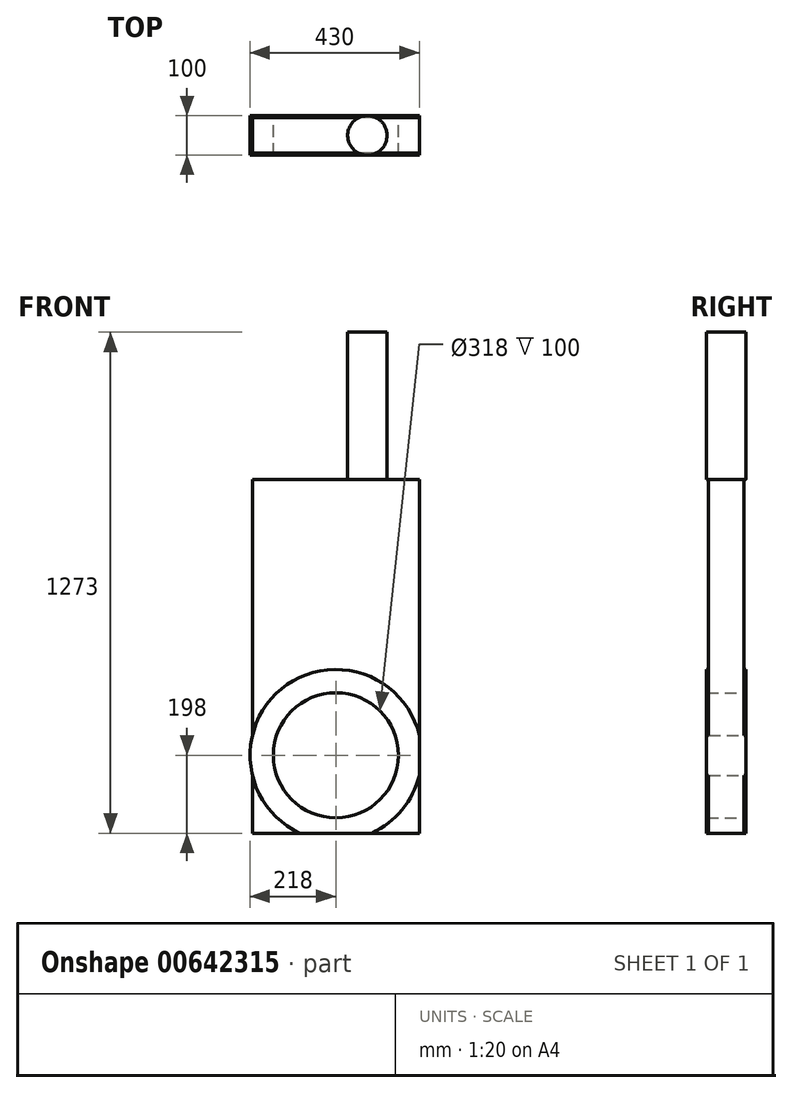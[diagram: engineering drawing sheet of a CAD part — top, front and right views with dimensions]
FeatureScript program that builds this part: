
annotation { "Feature Type Name" : "Feature", "Feature Type Description" : "" }
export const myFeature = defineFeature(function(context is Context, id is Id, definition is map)
    precondition{}
    {
        {
            var Q0;
            Q0=qCreatedBy(makeId("Front.planeOp"),FACE);
            var sketch = newSketch(context, id + "F0", { "sketchPlane" : qUnion([Q0])});
            skLineSegment(sketch, "E0.bottom", {"start": v(212, -449.5) * mm, "end": v(-212, -449.5) * mm});
            skLineSegment(sketch, "E0.top", {"start": v(212, 449.5) * mm, "end": v(-212, 449.5) * mm});
            skLineSegment(sketch, "E0.left", {"start": v(212, -449.5) * mm, "end": v(212, 449.5) * mm});
            skLineSegment(sketch, "E0.right", {"start": v(-212, -449.5) * mm, "end": v(-212, 449.5) * mm});
            skPoint(sketch, "E0.middle", {"position": v(0, 0) * mm});
            skSolve(sketch);
        }
        {
            var Q0;
            Q0=makeQuery(id+"F0.imprint","IMPRINT",FACE,{"disambiguationData":[TD([[makeQuery(id+"F0.imprint","IMPRINT",EDGE,{"derivedFrom":sQuery(id+"F0.wireOp",EDGE,"E0.bottom")}),-1.0]])]});
            extrude(context, id + "F1", {"entities" : qUnion([Q0]), "depth" : 90 * mm, "offsetDistance" : 25 * mm});
        }
        {
            var Q0;
            Q0=makeQuery(id+"F1.opExtrude","CAP_FACE",FACE,{"disambiguationData":[OSD([sQuery(id+"F0.wireOp",EDGE,"E0.bottom"),sQuery(id+"F0.wireOp",EDGE,"E0.top"),sQuery(id+"F0.wireOp",EDGE,"E0.left"),sQuery(id+"F0.wireOp",EDGE,"E0.right")])],"isStart":false});
            var sketch = newSketch(context, id + "F2", { "sketchPlane" : qUnion([Q0])});
            skCircle(sketch, "E1", {"center": v(0, -251.5) * mm, "radius": 218 * mm});
            skCircle(sketch, "E2", {"center": v(0, -251.5) * mm, "radius": 159 * mm});
            skSolve(sketch);
        }
        {
            var Q0;
            {var subQ0=sQuery(id+"F2.wireOp",EDGE,"E1");var subQ1=makeQuery(id+"F1.opExtrude","CAP_EDGE",EDGE,{"disambiguationData":[OSD([sQuery(id+"F0.wireOp",EDGE,"E0.right")])],"isStart":false});var subQ2=makeQuery(id+"F2.imprint","INTERSECT",VERTEX,{"disambiguationData":[OD(0.0)],"derivedFrom":[subQ1,subQ0]});Q0=makeQuery(id+"F2.imprint","IMPRINT",FACE,{"disambiguationData":[TD([[makeQuery(id+"F2.imprint","IMPRINT",EDGE,{"disambiguationData":[TD([[subQ2,-1.0]])],"derivedFrom":subQ0}),1.0]])]});}
            var Q1;
            Q1=makeQuery(id+"F2.imprint","IMPRINT",FACE,{"disambiguationData":[TD([[makeQuery(id+"F2.imprint","IMPRINT",EDGE,{"derivedFrom":sQuery(id+"F2.wireOp",EDGE,"E2")}),-1.0]])]});
            var Q2;
            {var subQ0=sQuery(id+"F2.wireOp",EDGE,"E1");var subQ1=makeQuery(id+"F1.opExtrude","CAP_EDGE",EDGE,{"disambiguationData":[OSD([sQuery(id+"F0.wireOp",EDGE,"E0.left")])],"isStart":false});var subQ2=makeQuery(id+"F2.imprint","INTERSECT",VERTEX,{"disambiguationData":[OD(0.0)],"derivedFrom":[subQ1,subQ0]});Q2=makeQuery(id+"F2.imprint","IMPRINT",FACE,{"disambiguationData":[TD([[makeQuery(id+"F2.imprint","IMPRINT",EDGE,{"disambiguationData":[TD([[subQ2,1.0]])],"derivedFrom":subQ0}),1.0]])]});}
            var Q3;
            {var subQ0=sQuery(id+"F2.wireOp",EDGE,"E1");var subQ1=makeQuery(id+"F1.opExtrude","CAP_EDGE",EDGE,{"disambiguationData":[OSD([sQuery(id+"F0.wireOp",EDGE,"E0.bottom")])],"isStart":false});var subQ2=makeQuery(id+"F2.imprint","INTERSECT",VERTEX,{"disambiguationData":[OD(0.0)],"derivedFrom":[subQ1,subQ0]});Q3=makeQuery(id+"F2.imprint","IMPRINT",FACE,{"disambiguationData":[TD([[makeQuery(id+"F2.imprint","IMPRINT",EDGE,{"disambiguationData":[TD([[subQ2,-1.0]])],"derivedFrom":subQ0}),1.0]])]});}
            extrude(context, id + "F3", {"entities" : qUnion([Q0, Q1, Q2, Q3]), "operationType" : NewBodyOperationType.ADD, "depth" : 5 * mm, "offsetDistance" : 25 * mm, "hasSecondDirection" : true, "secondDirectionOppositeDirection" : true, "secondDirectionDepth" : 95 * mm});
        }
        {
            var Q0;
            Q0=makeQuery(id+"F3.boolean.opBoolean","SPLIT",FACE,{"disambiguationData":[TD([makeQuery(id+"F3.opExtrude","SWEPT_FACE",FACE,{"disambiguationData":[OSD([sQuery(id+"F2.wireOp",EDGE,"E2")])]})])],"derivedFrom":makeQuery(id+"F1.opExtrude","CAP_FACE",FACE,{"disambiguationData":[OSD([sQuery(id+"F0.wireOp",EDGE,"E0.bottom"),sQuery(id+"F0.wireOp",EDGE,"E0.top"),sQuery(id+"F0.wireOp",EDGE,"E0.left"),sQuery(id+"F0.wireOp",EDGE,"E0.right")])],"isStart":false})});
            extrude(context, id + "F4", {"entities" : qUnion([Q0]), "operationType" : NewBodyOperationType.REMOVE, "endBound" : BoundingType.THROUGH_ALL, "oppositeDirection" : true, "depth" : 25 * mm, "offsetDistance" : 25 * mm});
        }
        {
            var Q0;
            Q0=makeQuery(id+"F1.opExtrude","SWEPT_FACE",FACE,{"disambiguationData":[OSD([sQuery(id+"F0.wireOp",EDGE,"E0.top")])]});
            var sketch = newSketch(context, id + "F5", { "sketchPlane" : qUnion([Q0])});
            skCircle(sketch, "E3", {"center": v(80, -45) * mm, "radius": 50 * mm});
            skPoint(sketch, "E3.centerSnap0", {"position": v(212, -45) * mm});
            skSolve(sketch);
        }
        {
            var Q0;
            {var subQ0=sQuery(id+"F5.wireOp",EDGE,"E3");var subQ1=makeQuery(id+"F1.opExtrude","CAP_EDGE",EDGE,{"disambiguationData":[OSD([sQuery(id+"F0.wireOp",EDGE,"E0.top")])],"isStart":true});var subQ2=makeQuery(id+"F5.imprint","INTERSECT",VERTEX,{"disambiguationData":[OD(0.0)],"derivedFrom":[subQ1,subQ0]});Q0=makeQuery(id+"F5.imprint","IMPRINT",FACE,{"disambiguationData":[TD([[makeQuery(id+"F5.imprint","IMPRINT",EDGE,{"disambiguationData":[TD([[subQ2,1.0]])],"derivedFrom":subQ0}),1.0]])]});}
            var Q1;
            {var subQ0=sQuery(id+"F5.wireOp",EDGE,"E3");var subQ1=makeQuery(id+"F1.opExtrude","CAP_EDGE",EDGE,{"disambiguationData":[OSD([sQuery(id+"F0.wireOp",EDGE,"E0.top")])],"isStart":false});var subQ2=makeQuery(id+"F5.imprint","INTERSECT",VERTEX,{"disambiguationData":[OD(0.0)],"derivedFrom":[subQ1,subQ0]});Q1=makeQuery(id+"F5.imprint","IMPRINT",FACE,{"disambiguationData":[TD([[makeQuery(id+"F5.imprint","IMPRINT",EDGE,{"disambiguationData":[TD([[subQ2,-1.0]])],"derivedFrom":subQ0}),1.0]])]});}
            var Q2;
            {var subQ0=sQuery(id+"F5.wireOp",EDGE,"E3");var subQ1=sQuery(id+"F0.wireOp",EDGE,"E0.top");var subQ2=makeQuery(id+"F1.opExtrude","CAP_EDGE",EDGE,{"disambiguationData":[OSD([subQ1])],"isStart":true});var subQ3=makeQuery(id+"F5.imprint","INTERSECT",VERTEX,{"disambiguationData":[OD(0.0)],"derivedFrom":[subQ2,subQ0]});Q2=makeQuery(id+"F5.imprint","IMPRINT",FACE,{"disambiguationData":[TD([[makeQuery(id+"F5.imprint","IMPRINT",EDGE,{"disambiguationData":[TD([[subQ3,-1.0]])],"derivedFrom":subQ0}),1.0]])]});}
            extrude(context, id + "F6", {"entities" : qUnion([Q0, Q1, Q2]), "operationType" : NewBodyOperationType.ADD, "depth" : (1075 - 701) * mm, "offsetDistance" : 25 * mm});
        }
    });
